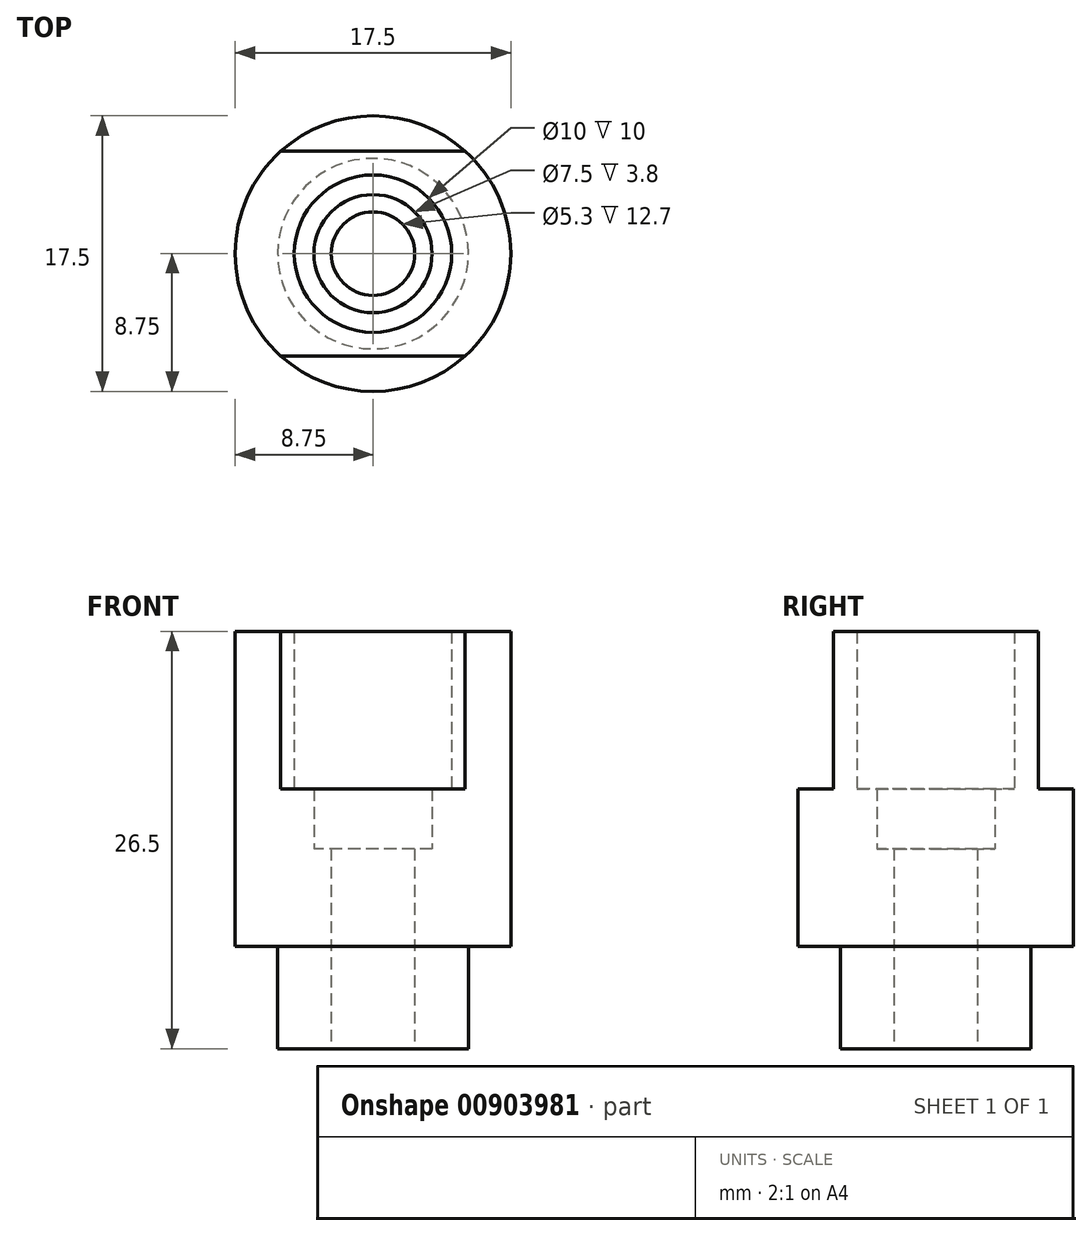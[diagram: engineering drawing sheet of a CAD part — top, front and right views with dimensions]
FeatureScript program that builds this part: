
annotation { "Feature Type Name" : "Feature", "Feature Type Description" : "" }
export const myFeature = defineFeature(function(context is Context, id is Id, definition is map)
    precondition{}
    {
        {
            var Q0;
            Q0=qCreatedBy(makeId("Top.planeOp"),FACE);
            var sketch = newSketch(context, id + "F0", { "sketchPlane" : qUnion([Q0])});
            skCircle(sketch, "E0", {"center": v(0, 0) * mm, "radius": 8.75 * mm});
            skCircle(sketch, "E1", {"center": v(0, 0) * mm, "radius": 2.65 * mm});
            skCircle(sketch, "E2", {"center": v(0, 0) * mm, "radius": 3.75 * mm});
            skCircle(sketch, "E3", {"center": v(0, 0) * mm, "radius": 5 * mm});
            skCircle(sketch, "E4", {"center": v(0, 0) * mm, "radius": 6.05 * mm});
            skSolve(sketch);
        }
        {
            var Q0;
            Q0=makeQuery(id+"F0.imprint","IMPRINT",FACE,{"disambiguationData":[TD([[makeQuery(id+"F0.imprint","IMPRINT",EDGE,{"derivedFrom":sQuery(id+"F0.wireOp",EDGE,"E0")}),1.0]])]});
            var Q1;
            Q1=makeQuery(id+"F0.imprint","IMPRINT",FACE,{"disambiguationData":[TD([[makeQuery(id+"F0.imprint","IMPRINT",EDGE,{"derivedFrom":sQuery(id+"F0.wireOp",EDGE,"E3")}),-1.0]])]});
            extrude(context, id + "F1", {"entities" : qUnion([Q0, Q1]), "depth" : 20 * mm, "offsetDistance" : 25 * mm});
        }
        {
            var Q0;
            Q0=makeQuery(id+"F0.imprint","IMPRINT",FACE,{"disambiguationData":[TD([[makeQuery(id+"F0.imprint","IMPRINT",EDGE,{"derivedFrom":sQuery(id+"F0.wireOp",EDGE,"E2")}),-1.0]])]});
            extrude(context, id + "F2", {"entities" : qUnion([Q0]), "depth" : 10 * mm, "offsetDistance" : 25 * mm});
        }
        {
            var Q0;
            Q0=makeQuery(id+"F0.imprint","IMPRINT",FACE,{"disambiguationData":[TD([[makeQuery(id+"F0.imprint","IMPRINT",EDGE,{"derivedFrom":sQuery(id+"F0.wireOp",EDGE,"E1")}),-1.0]])]});
            extrude(context, id + "F3", {"entities" : qUnion([Q0]), "operationType" : NewBodyOperationType.ADD, "depth" : (10 - 3.8) * mm, "offsetDistance" : 25 * mm});
        }
        {
            var Q0;
            Q0=makeQuery(id+"F1.opExtrude","CAP_FACE",FACE,{"disambiguationData":[OSD([sQuery(id+"F0.wireOp",EDGE,"E0"),sQuery(id+"F0.wireOp",EDGE,"E3")])],"isStart":false});
            var sketch = newSketch(context, id + "F4", { "sketchPlane" : qUnion([Q0])});
            skLineSegment(sketch, "E5.bottom", {"start": v(12.5, 6.5) * mm, "end": v(-12.5, 6.5) * mm});
            skLineSegment(sketch, "E5.top", {"start": v(12.5, -6.5) * mm, "end": v(-12.5, -6.5) * mm});
            skLineSegment(sketch, "E5.left", {"start": v(12.5, 6.5) * mm, "end": v(12.5, -6.5) * mm});
            skLineSegment(sketch, "E5.right", {"start": v(-12.5, 6.5) * mm, "end": v(-12.5, -6.5) * mm});
            skPoint(sketch, "E5.middle", {"position": v(0, 0) * mm});
            skSolve(sketch);
        }
        {
            var Q0;
            {var subQ0=sQuery(id+"F4.wireOp",EDGE,"E5.top");var subQ1=makeQuery(id+"F1.opExtrude","CAP_EDGE",EDGE,{"disambiguationData":[OSD([sQuery(id+"F0.wireOp",EDGE,"E0")])],"isStart":false});var subQ2=makeQuery(id+"F4.imprint","INTERSECT",VERTEX,{"disambiguationData":[OD(0.0)],"derivedFrom":[subQ1,subQ0]});Q0=makeQuery(id+"F4.imprint","IMPRINT",FACE,{"disambiguationData":[TD([[makeQuery(id+"F4.imprint","IMPRINT",EDGE,{"disambiguationData":[TD([[subQ2,-1.0]])],"derivedFrom":subQ0}),1.0]])]});}
            var Q1;
            {var subQ0=sQuery(id+"F4.wireOp",EDGE,"E5.bottom");var subQ1=makeQuery(id+"F1.opExtrude","CAP_EDGE",EDGE,{"disambiguationData":[OSD([sQuery(id+"F0.wireOp",EDGE,"E0")])],"isStart":false});var subQ2=makeQuery(id+"F4.imprint","INTERSECT",VERTEX,{"disambiguationData":[OD(0.0)],"derivedFrom":[subQ1,subQ0]});Q1=makeQuery(id+"F4.imprint","IMPRINT",FACE,{"disambiguationData":[TD([[makeQuery(id+"F4.imprint","IMPRINT",EDGE,{"disambiguationData":[TD([[subQ2,-1.0]])],"derivedFrom":subQ0}),-1.0]])]});}
            extrude(context, id + "F5", {"entities" : qUnion([Q0, Q1]), "operationType" : NewBodyOperationType.REMOVE, "oppositeDirection" : true, "depth" : 10 * mm, "offsetDistance" : 25 * mm});
        }
        {
            var Q0;
            Q0=makeQuery(id+"F0.imprint","IMPRINT",FACE,{"disambiguationData":[TD([[makeQuery(id+"F0.imprint","IMPRINT",EDGE,{"derivedFrom":sQuery(id+"F0.wireOp",EDGE,"E3")}),-1.0]])]});
            var Q1;
            Q1=makeQuery(id+"F0.imprint","IMPRINT",FACE,{"disambiguationData":[TD([[makeQuery(id+"F0.imprint","IMPRINT",EDGE,{"derivedFrom":sQuery(id+"F0.wireOp",EDGE,"E2")}),-1.0]])]});
            var Q2;
            Q2=makeQuery(id+"F0.imprint","IMPRINT",FACE,{"disambiguationData":[TD([[makeQuery(id+"F0.imprint","IMPRINT",EDGE,{"derivedFrom":sQuery(id+"F0.wireOp",EDGE,"E1")}),-1.0]])]});
            extrude(context, id + "F6", {"entities" : qUnion([Q0, Q1, Q2]), "operationType" : NewBodyOperationType.ADD, "oppositeDirection" : true, "depth" : 6.5 * mm, "offsetDistance" : 25 * mm});
        }
    });
